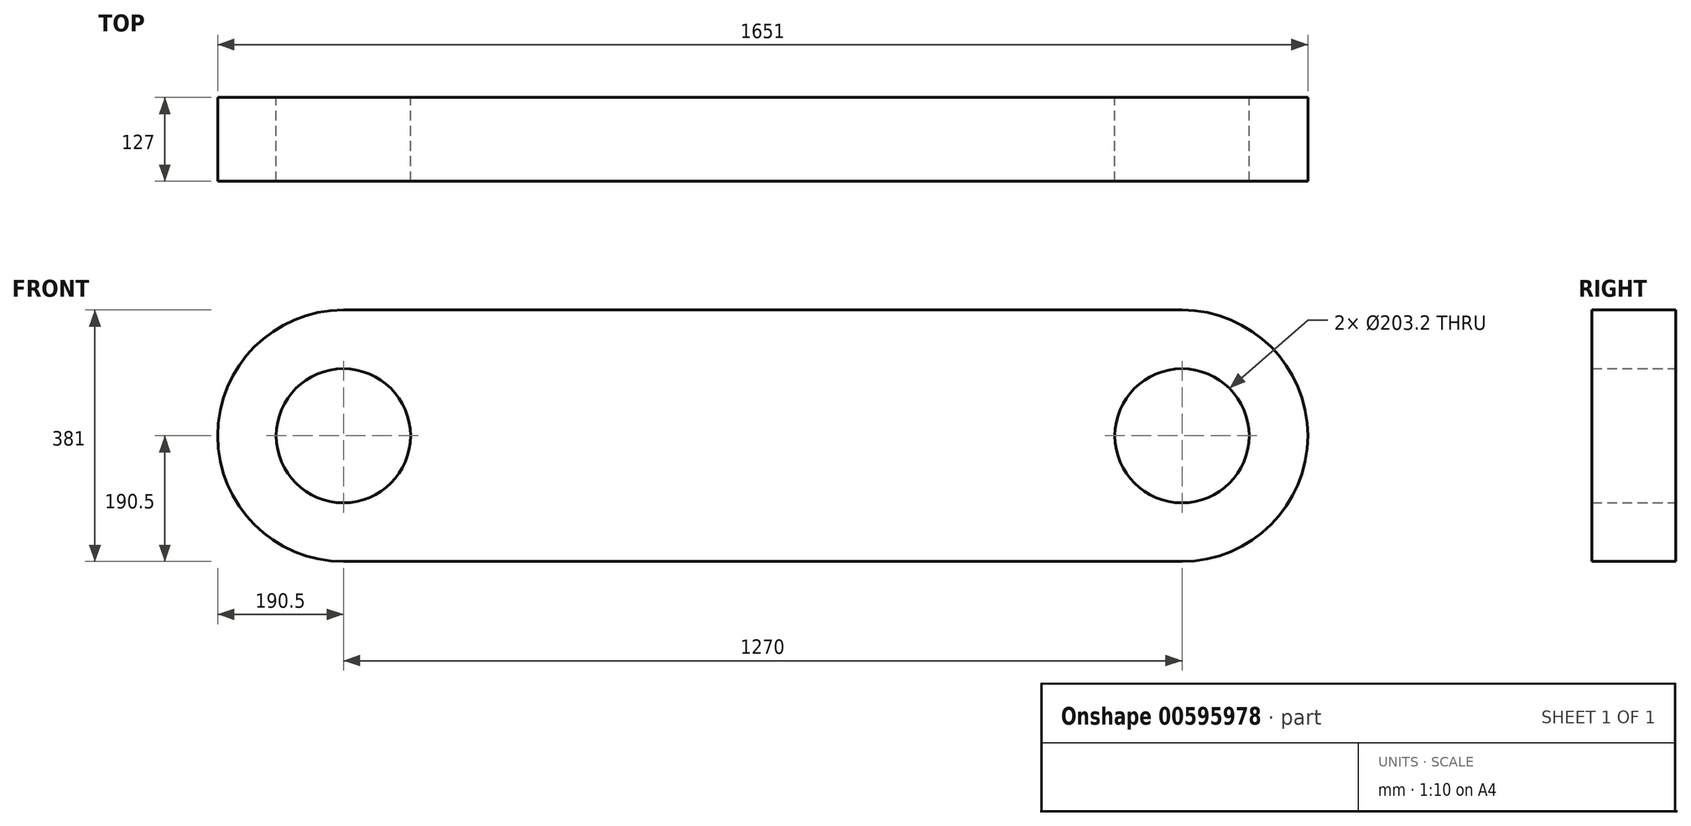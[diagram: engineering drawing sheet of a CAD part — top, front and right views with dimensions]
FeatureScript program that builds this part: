
annotation { "Feature Type Name" : "Feature", "Feature Type Description" : "" }
export const myFeature = defineFeature(function(context is Context, id is Id, definition is map)
    precondition{}
    {
        {
            var Q0;
            Q0=qCreatedBy(makeId("Front.planeOp"),FACE);
            var sketch = newSketch(context, id + "F0", { "sketchPlane" : qUnion([Q0])});
            skArc(sketch, "E0", {"start": v(0, 190.5) * mm, "mid": v(-190.5, 0) * mm, "end": v(0, -190.5) * mm});
            skArc(sketch, "E1", {"start": v(1270, -190.5) * mm, "mid": v(1460.5, 0) * mm, "end": v(1270, 190.5) * mm});
            skLineSegment(sketch, "E2", {"start": v(0, 190.5) * mm, "end": v(1270, 190.5) * mm});
            skLineSegment(sketch, "E3", {"start": v(0, -190.5) * mm, "end": v(1270, -190.5) * mm});
            skCircle(sketch, "E4", {"center": v(0, 0) * mm, "radius": 101.6 * mm});
            skCircle(sketch, "E5", {"center": v(1270, 0) * mm, "radius": 101.6 * mm});
            skSolve(sketch);
        }
        {
            var Q0;
            Q0=makeQuery(id+"F0.imprint","IMPRINT",FACE,{"disambiguationData":[TD([[makeQuery(id+"F0.imprint","IMPRINT",EDGE,{"derivedFrom":sQuery(id+"F0.wireOp",EDGE,"E0")}),1.0]])]});
            extrude(context, id + "F1", {"entities" : qUnion([Q0]), "depth" : 127 * mm, "offsetDistance" : 25.4 * mm});
        }
    });
